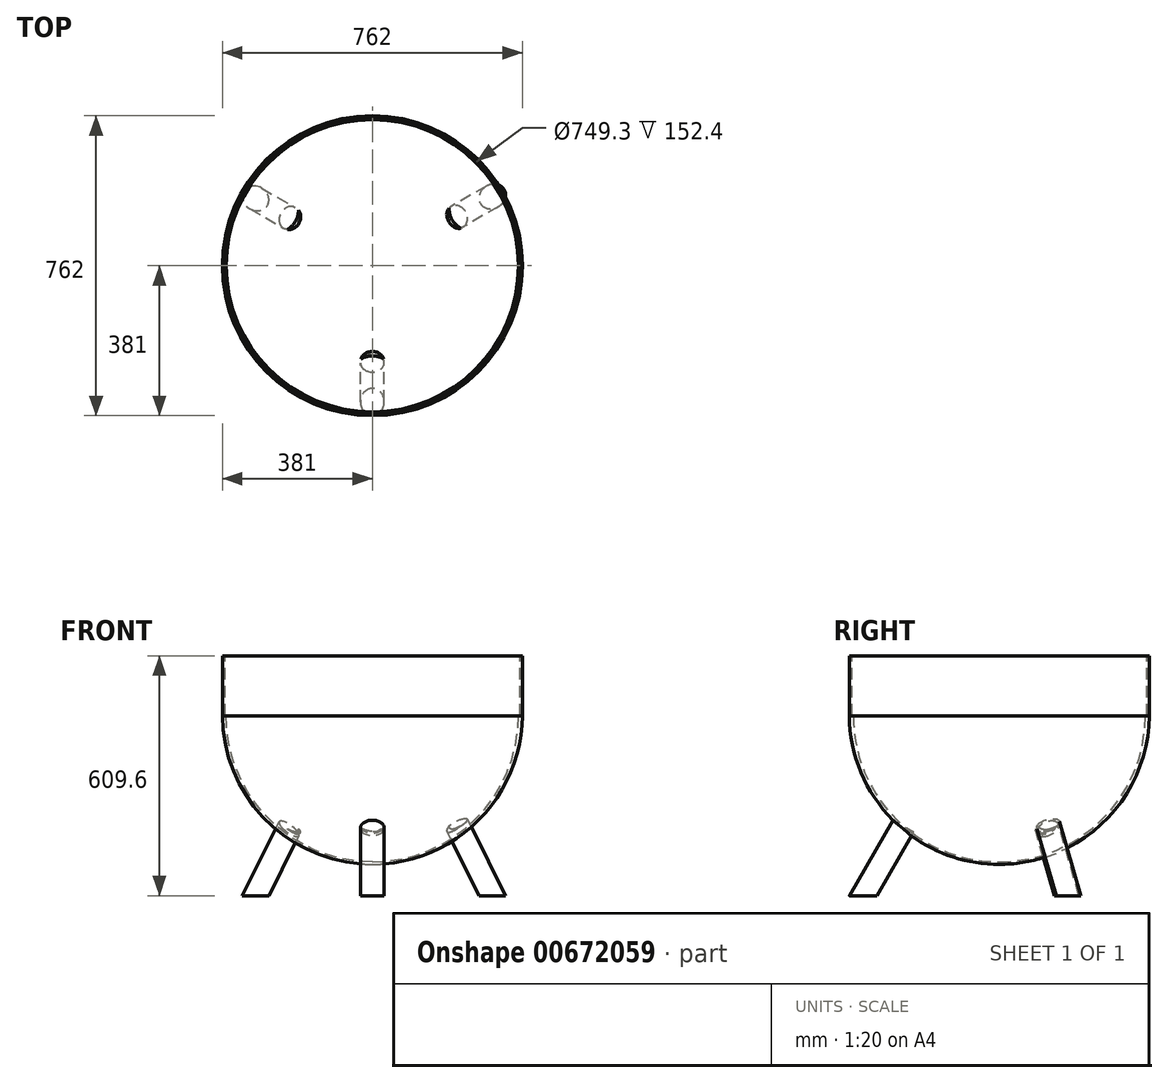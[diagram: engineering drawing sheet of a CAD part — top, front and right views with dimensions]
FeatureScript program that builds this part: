
annotation { "Feature Type Name" : "Feature", "Feature Type Description" : "" }
export const myFeature = defineFeature(function(context is Context, id is Id, definition is map)
    precondition{}
    {
        {
            var Q0;
            Q0=qCreatedBy(makeId("Top.planeOp"),FACE);
            var sketch = newSketch(context, id + "F0", { "sketchPlane" : qUnion([Q0])});
            skCircle(sketch, "E0.cCircle", {"center": v(0, 0) * mm, "radius": 527.93 * mm, "construction": true});
            skLineSegment(sketch, "E0.0", {"start": v(304.8, 527.93) * mm, "end": v(609.6, 0) * mm});
            skLineSegment(sketch, "E0.1", {"start": v(609.6, 0) * mm, "end": v(457.2, -263.96) * mm});
            skLineSegment(sketch, "E0.2", {"start": v(304.8, -527.93) * mm, "end": v(-304.8, -527.93) * mm});
            skLineSegment(sketch, "E0.3", {"start": v(-304.8, -527.93) * mm, "end": v(-457.2, -263.96) * mm});
            skLineSegment(sketch, "E0.4", {"start": v(-609.6, 0) * mm, "end": v(-450.85, 274.96) * mm});
            skLineSegment(sketch, "E0.5", {"start": v(-304.8, 527.93) * mm, "end": v(0, 527.93) * mm});
            skPoint(sketch, "E0.0.midPoint", {"position": v(457.2, 263.96) * mm});
            skCircle(sketch, "E1", {"center": v(0, 0) * mm, "radius": 381 * mm});
            skLineSegment(sketch, "E2", {"start": v(-463.55, 252.97) * mm, "end": v(-336.12, 179.4) * mm});
            skLineSegment(sketch, "E3", {"start": v(-450.85, 274.96) * mm, "end": v(-323.42, 201.4) * mm});
            skLineSegment(sketch, "E4", {"start": v(-304.8, 527.93) * mm, "end": v(-304.8, 527.93) * mm});
            skLineSegment(sketch, "E5", {"start": v(-463.55, 252.97) * mm, "end": v(-304.8, 527.93) * mm});
            skLineSegment(sketch, "E6", {"start": v(-450.85, 274.96) * mm, "end": v(-401.2, 360.95) * mm});
            skLineSegment(sketch, "E7", {"start": v(-609.6, 0) * mm, "end": v(-609.6, 0) * mm});
            skLineSegment(sketch, "E8.1.0", {"start": v(-450.85, -274.96) * mm, "end": v(-323.42, -201.4) * mm});
            skLineSegment(sketch, "E8.1.1", {"start": v(-463.55, -252.97) * mm, "end": v(-336.12, -179.4) * mm});
            skLineSegment(sketch, "E8.2.0", {"start": v(12.7, -527.93) * mm, "end": v(12.7, -380.79) * mm});
            skLineSegment(sketch, "E8.2.1", {"start": v(-12.7, -527.93) * mm, "end": v(-12.7, -380.79) * mm});
            skLineSegment(sketch, "E8.3.0", {"start": v(463.55, -252.97) * mm, "end": v(336.12, -179.4) * mm});
            skLineSegment(sketch, "E8.3.1", {"start": v(450.85, -274.96) * mm, "end": v(323.42, -201.4) * mm});
            skLineSegment(sketch, "E8.4.0", {"start": v(450.85, 274.96) * mm, "end": v(323.42, 201.4) * mm});
            skLineSegment(sketch, "E8.4.1", {"start": v(463.55, 252.97) * mm, "end": v(336.12, 179.4) * mm});
            skLineSegment(sketch, "E8.5.0", {"start": v(-12.7, 527.93) * mm, "end": v(-12.7, 380.79) * mm});
            skLineSegment(sketch, "E8.5.1", {"start": v(12.7, 527.93) * mm, "end": v(12.7, 380.79) * mm});
            skLineSegment(sketch, "E9", {"start": v(-1099.5, 381) * mm, "end": v(1284.02, 381) * mm, "construction": true});
            skLineSegment(sketch, "E10", {"start": v(-1101.82, -381) * mm, "end": v(1466.6, -381) * mm, "construction": true});
            skLineSegment(sketch, "E11", {"start": v(127, -73.32) * mm, "end": v(-127, -73.32) * mm});
            skCircle(sketch, "E12", {"center": v(0, 0) * mm, "radius": 146.65 * mm, "construction": true});
            skLineSegment(sketch, "E13", {"start": v(0, 0) * mm, "end": v(329.96, -190.5) * mm, "construction": true});
            skLineSegment(sketch, "E14", {"start": v(0, 0) * mm, "end": v(-329.96, -190.5) * mm, "construction": true});
            skLineSegment(sketch, "E15", {"start": v(0, 0) * mm, "end": v(0, 381) * mm, "construction": true});
            skLineSegment(sketch, "E16", {"start": v(329.96, -190.5) * mm, "end": v(1171.58, -676.41) * mm, "construction": true});
            skLineSegment(sketch, "E17", {"start": v(457.2, -263.96) * mm, "end": v(304.8, -527.93) * mm});
            skLineSegment(sketch, "E18", {"start": v(329.96, -190.5) * mm, "end": v(457.2, -263.96) * mm});
            skLineSegment(sketch, "E19", {"start": v(0, 381) * mm, "end": v(0, 1090.4) * mm, "construction": true});
            skLineSegment(sketch, "E20", {"start": v(0, 527.93) * mm, "end": v(304.8, 527.93) * mm});
            skLineSegment(sketch, "E21", {"start": v(0, 527.93) * mm, "end": v(0, 381) * mm});
            skLineSegment(sketch, "E22", {"start": v(-329.96, -190.5) * mm, "end": v(-1262.9, -729.14) * mm, "construction": true});
            skLineSegment(sketch, "E23", {"start": v(-457.2, -263.96) * mm, "end": v(-609.6, 0) * mm});
            skLineSegment(sketch, "E24", {"start": v(-329.96, -190.5) * mm, "end": v(-457.2, -263.96) * mm});
            skCircle(sketch, "E25", {"center": v(0, 0) * mm, "radius": 374.65 * mm});
            skSolve(sketch);
        }
        {
            var Q0;
            {var subQ0=sQuery(id+"F0.wireOp",EDGE,"E1");var subQ8=makeQuery(id+"F0.imprint","INTERSECT",VERTEX,{"derivedFrom":[subQ0,sQuery(id+"F0.wireOp",EDGE,"E8.4.0")]});Q0=makeQuery(id+"F0.imprint","IMPRINT",FACE,{"disambiguationData":[TD([[makeQuery(id+"F0.imprint","IMPRINT",EDGE,{"disambiguationData":[TD([[subQ8,1.0]])],"derivedFrom":subQ0}),1.0]])]});}
            extrude(context, id + "F1", {"entities" : qUnion([Q0]), "oppositeDirection" : true, "depth" : 152.4 * mm, "offsetDistance" : 25.4 * mm, "hasSecondDirection" : true, "secondDirectionOppositeDirection" : true, "secondDirectionDepth" : 0 * mm});
        }
        {
            var Q0;
            Q0=qCreatedBy(makeId("Front.planeOp"),FACE);
            var sketch = newSketch(context, id + "F2", { "sketchPlane" : qUnion([Q0])});
            skLineSegment(sketch, "E26", {"start": v(0, 608.83) * mm, "end": v(0, -1105.26) * mm, "construction": true});
            skLineSegment(sketch, "E27", {"start": v(-381, 462.6) * mm, "end": v(-381, -843.09) * mm});
            skLineSegment(sketch, "E28.MirrorCS", {"start": v(381, 462.6) * mm, "end": v(381, -843.09) * mm});
            skLineSegment(sketch, "E29", {"start": v(-1108.33, -152.4) * mm, "end": v(1492.5, -152.4) * mm, "construction": true});
            skArc(sketch, "E30", {"start": v(-381, -152.4) * mm, "mid": v(-268.19, -419.57) * mm, "end": v(0, -529.94) * mm});
            skArc(sketch, "E31", {"start": v(0, -529.94) * mm, "mid": v(268.19, -419.57) * mm, "end": v(381, -152.4) * mm});
            skLineSegment(sketch, "E32", {"start": v(-495.68, -152.4) * mm, "end": v(0, -152.4) * mm});
            skLineSegment(sketch, "E33", {"start": v(0, 45.3) * mm, "end": v(0, -541.67) * mm});
            skLineSegment(sketch, "E34", {"start": v(0, -152.4) * mm, "end": v(518.85, -152.4) * mm});
            skCircle(sketch, "E35", {"center": v(0, -152.4) * mm, "radius": 371.19 * mm});
            skSolve(sketch);
        }
        {
            var Q0;
            Q0=sQuery(id+"F0.wireOp",EDGE,"E13");
            var Q1;
            Q1=sQuery(id+"F2.wireOp",EDGE,"E26");
            cPlane(context, id + "F3", {"entities" : qUnion([Q0, Q1]), "cplaneType" : CPlaneType.LINE_ANGLE, "offset" : 25.4 * mm, "angle" : 0 * degree, "width" : 152.4 * mm, "height" : 152.4 * mm});
        }
        {
            var Q0;
            Q0=sQuery(id+"F0.wireOp",EDGE,"E15");
            var Q1;
            Q1=sQuery(id+"F2.wireOp",EDGE,"E26");
            cPlane(context, id + "F4", {"entities" : qUnion([Q0, Q1]), "cplaneType" : CPlaneType.LINE_ANGLE, "offset" : 25.4 * mm, "angle" : 0 * degree, "width" : 152.4 * mm, "height" : 152.4 * mm});
        }
        {
            var Q0;
            Q0=sQuery(id+"F0.wireOp",EDGE,"E22");
            var Q1;
            Q1=sQuery(id+"F2.wireOp",EDGE,"E26");
            cPlane(context, id + "F5", {"entities" : qUnion([Q0, Q1]), "cplaneType" : CPlaneType.LINE_ANGLE, "offset" : 25.4 * mm, "angle" : 0 * degree, "width" : 152.4 * mm, "height" : 152.4 * mm});
        }
        {
            var Q0;
            Q0=qCreatedBy(id+"F5.planeOp",FACE);
            var sketch = newSketch(context, id + "F6", { "sketchPlane" : qUnion([Q0])});
            skLineSegment(sketch, "E36", {"start": v(-1017.96, -609.6) * mm, "end": v(-351.95, -609.6) * mm});
            skLineSegment(sketch, "E37", {"start": v(-2207.22, 0) * mm, "end": v(364.68, 0) * mm, "construction": true});
            skLineSegment(sketch, "E38", {"start": v(0, 853.8) * mm, "end": v(0, -860.28) * mm, "construction": true});
            skLineSegment(sketch, "E39", {"start": v(-381, 707.57) * mm, "end": v(-381, -944.4) * mm});
            skLineSegment(sketch, "E40", {"start": v(-2225.52, -152.4) * mm, "end": v(0, -152.4) * mm, "construction": true});
            skArc(sketch, "E41", {"start": v(-381, -152.4) * mm, "mid": v(-268.19, -419.57) * mm, "end": v(0, -529.94) * mm});
            skArc(sketch, "E42", {"start": v(0, -529.94) * mm, "mid": v(268.19, -419.57) * mm, "end": v(381, -152.4) * mm});
            skLineSegment(sketch, "E43", {"start": v(0, -152.4) * mm, "end": v(375.32, -152.4) * mm, "construction": true});
            skLineSegment(sketch, "E44", {"start": v(-1487.46, 0) * mm, "end": v(0, 0) * mm, "construction": true});
            skLineSegment(sketch, "E45", {"start": v(-470.85, 0) * mm, "end": v(0, 0) * mm, "construction": true});
            skLineSegment(sketch, "E46", {"start": v(277.13, -609.6) * mm, "end": v(310.58, -609.6) * mm});
            skLineSegment(sketch, "E47", {"start": v(0, 0) * mm, "end": v(-351.95, -609.6) * mm});
            skLineSegment(sketch, "E48", {"start": v(32.55, -3.98) * mm, "end": v(-317.1, -609.6) * mm});
            skLineSegment(sketch, "E49", {"start": v(-34.84, 0) * mm, "end": v(-386.8, -609.6) * mm});
            skLineSegment(sketch, "E50", {"start": v(-381, -609.6) * mm, "end": v(1871, -609.6) * mm});
            skLineSegment(sketch, "E51.MirrorCS", {"start": v(34.84, 0) * mm, "end": v(386.8, -609.6) * mm});
            skLineSegment(sketch, "E52.MirrorCS", {"start": v(-32.55, -3.98) * mm, "end": v(317.1, -609.6) * mm});
            skLineSegment(sketch, "E53.MirrorCS", {"start": v(0, 0) * mm, "end": v(351.95, -609.6) * mm});
            skSolve(sketch);
        }
        {
            var Q0;
            {var subQ0=sQuery(id+"F6.wireOp",EDGE,"E51.MirrorCS");var subQ1=sQuery(id+"F6.wireOp",EDGE,"E42");var subQ2=makeQuery(id+"F6.imprint","INTERSECT",VERTEX,{"derivedFrom":[subQ1,subQ0]});Q0=makeQuery(id+"F6.imprint","IMPRINT",FACE,{"disambiguationData":[TD([[makeQuery(id+"F6.imprint","IMPRINT",EDGE,{"disambiguationData":[TD([[subQ2,1.0]])],"derivedFrom":subQ1}),-1.0]])]});}
            var Q1;
            Q1=sQuery(id+"F6.wireOp",EDGE,"E53.MirrorCS");
            revolve(context, id + "F7", {"entities" : qUnion([Q0]), "axis" : qUnion([Q1]), "revolveType" : RevolveType.FULL});
        }
        {
            var Q0;
            {var subQ0=sQuery(id+"F2.wireOp",EDGE,"E31");Q0=makeQuery(id+"F2.imprint","IMPRINT",FACE,{"disambiguationData":[TD([[makeQuery(id+"F2.imprint","IMPRINT",EDGE,{"derivedFrom":subQ0}),1.0]])]});}
            var Q1;
            Q1=sQuery(id+"F2.wireOp",EDGE,"E33");
            revolve(context, id + "F8", {"entities" : qUnion([Q0]), "axis" : qUnion([Q1]), "revolveType" : RevolveType.FULL});
        }
        {
            var Q0;
            {var subQ0=sQuery(id+"F2.wireOp",EDGE,"E34");var subQ3=sQuery(id+"F2.wireOp",EDGE,"E35");var subQ5=makeQuery(id+"F2.imprint","INTERSECT",VERTEX,{"derivedFrom":[subQ0,subQ3]});Q0=makeQuery(id+"F2.imprint","IMPRINT",FACE,{"disambiguationData":[TD([[makeQuery(id+"F2.imprint","IMPRINT",EDGE,{"disambiguationData":[TD([[subQ5,1.0]])],"derivedFrom":subQ3}),1.0]])]});}
            var Q1;
            Q1=sQuery(id+"F2.wireOp",EDGE,"E33");
            revolve(context, id + "F9", {"operationType" : NewBodyOperationType.REMOVE, "entities" : qUnion([Q0]), "axis" : qUnion([Q1]), "revolveType" : RevolveType.FULL, "oppositeDirection" : true});
        }
        {
            var Q0;
            {var subQ0=sQuery(id+"F0.wireOp",EDGE,"E8.1.0");Q0=makeQuery(id+"F0.imprint","IMPRINT",FACE,{"disambiguationData":[TD([[makeQuery(id+"F0.imprint","IMPRINT",EDGE,{"derivedFrom":subQ0}),-1.0]])]});}
            cPlane(context, id + "F10", {"entities" : qUnion([Q0]), "cplaneType" : CPlaneType.OFFSET, "offset" : 647.7 * mm, "oppositeDirection" : true, "width" : 152.4 * mm, "height" : 152.4 * mm});
        }
        {
            var Q0;
            Q0=qCreatedBy(id+"F10.planeOp",FACE);
            var sketch = newSketch(context, id + "F11", { "sketchPlane" : qUnion([Q0])});
            skLineSegment(sketch, "E54.bottom", {"start": v(-408.5, 256.07) * mm, "end": v(423.7, 256.07) * mm});
            skLineSegment(sketch, "E54.top", {"start": v(-408.5, -410.84) * mm, "end": v(423.7, -410.84) * mm});
            skLineSegment(sketch, "E54.left", {"start": v(-408.5, 256.07) * mm, "end": v(-408.5, -410.84) * mm});
            skLineSegment(sketch, "E54.right", {"start": v(423.7, 256.07) * mm, "end": v(423.7, -410.84) * mm});
            skSolve(sketch);
        }
        {
            var Q0;
            Q0=qSketchRegion(id+"F11",true);
            extrude(context, id + "F12", {"entities" : qUnion([Q0]), "operationType" : NewBodyOperationType.REMOVE, "oppositeDirection" : true, "depth" : 50.8 * mm, "offsetDistance" : 25.4 * mm});
        }
        {
            var Q0;
            Q0=qCreatedBy(id+"F3.planeOp",FACE);
            var sketch = newSketch(context, id + "F13", { "sketchPlane" : qUnion([Q0])});
            skLineSegment(sketch, "E55", {"start": v(-1049.37, -609.6) * mm, "end": v(-342.54, -609.6) * mm});
            skLineSegment(sketch, "E56", {"start": v(-2238.63, 0) * mm, "end": v(333.27, 0) * mm, "construction": true});
            skLineSegment(sketch, "E57", {"start": v(0, 853.8) * mm, "end": v(0, -860.28) * mm, "construction": true});
            skLineSegment(sketch, "E58", {"start": v(-381, 707.57) * mm, "end": v(-381, -944.4) * mm});
            skLineSegment(sketch, "E59", {"start": v(-2225.52, -152.4) * mm, "end": v(0, -152.4) * mm, "construction": true});
            skArc(sketch, "E60", {"start": v(-381, -152.4) * mm, "mid": v(-268.19, -419.57) * mm, "end": v(0, -529.94) * mm});
            skArc(sketch, "E61", {"start": v(0, -529.94) * mm, "mid": v(268.19, -419.57) * mm, "end": v(381, -152.4) * mm});
            skLineSegment(sketch, "E62", {"start": v(0, -152.4) * mm, "end": v(375.32, -152.4) * mm, "construction": true});
            skLineSegment(sketch, "E63", {"start": v(-1518.87, 0) * mm, "end": v(0, 0) * mm, "construction": true});
            skLineSegment(sketch, "E64", {"start": v(-502.26, 0) * mm, "end": v(0, 0) * mm, "construction": true});
            skLineSegment(sketch, "E65", {"start": v(245.72, -609.6) * mm, "end": v(310.58, -609.6) * mm});
            skLineSegment(sketch, "E66", {"start": v(9.41, 0) * mm, "end": v(-342.54, -609.6) * mm});
            skLineSegment(sketch, "E67", {"start": v(63.96, 34.12) * mm, "end": v(-307.7, -609.6) * mm});
            skLineSegment(sketch, "E68", {"start": v(-25.43, 0) * mm, "end": v(-377.38, -609.6) * mm});
            skLineSegment(sketch, "E69", {"start": v(-381, -609.6) * mm, "end": v(1839.6, -609.6) * mm});
            skLineSegment(sketch, "E70.MirrorCS", {"start": v(25.43, 0) * mm, "end": v(377.38, -609.6) * mm});
            skLineSegment(sketch, "E71.MirrorCS", {"start": v(-63.96, 34.12) * mm, "end": v(307.7, -609.6) * mm});
            skLineSegment(sketch, "E72.MirrorCS", {"start": v(-9.41, 0) * mm, "end": v(342.54, -609.6) * mm});
            skSolve(sketch);
        }
        {
            var Q0;
            {var subQ0=sQuery(id+"F13.wireOp",EDGE,"E70.MirrorCS");var subQ1=sQuery(id+"F13.wireOp",EDGE,"E61");var subQ2=makeQuery(id+"F13.imprint","INTERSECT",VERTEX,{"derivedFrom":[subQ1,subQ0]});Q0=makeQuery(id+"F13.imprint","IMPRINT",FACE,{"disambiguationData":[TD([[makeQuery(id+"F13.imprint","IMPRINT",EDGE,{"disambiguationData":[TD([[subQ2,1.0]])],"derivedFrom":subQ1}),-1.0]])]});}
            var Q1;
            Q1=sQuery(id+"F13.wireOp",EDGE,"E72.MirrorCS");
            revolve(context, id + "F14", {"operationType" : NewBodyOperationType.ADD, "entities" : qUnion([Q0]), "axis" : qUnion([Q1]), "revolveType" : RevolveType.FULL});
        }
        {
            var Q0;
            Q0=qCreatedBy(id+"F4.planeOp",FACE);
            var sketch = newSketch(context, id + "F15", { "sketchPlane" : qUnion([Q0])});
            skLineSegment(sketch, "E73", {"start": v(-1075.54, -609.6) * mm, "end": v(-346.16, -609.6) * mm});
            skLineSegment(sketch, "E74", {"start": v(-2264.8, 0) * mm, "end": v(307.1, 0) * mm, "construction": true});
            skLineSegment(sketch, "E75", {"start": v(0, 1137.28) * mm, "end": v(0, -576.81) * mm, "construction": true});
            skLineSegment(sketch, "E76", {"start": v(-381, 707.57) * mm, "end": v(-381, -944.4) * mm});
            skLineSegment(sketch, "E77", {"start": v(-2225.52, -152.4) * mm, "end": v(0, -152.4) * mm, "construction": true});
            skArc(sketch, "E78", {"start": v(-381, -152.4) * mm, "mid": v(-268.19, -419.57) * mm, "end": v(0, -529.94) * mm});
            skArc(sketch, "E79", {"start": v(0, -529.94) * mm, "mid": v(268.19, -419.57) * mm, "end": v(381, -152.4) * mm});
            skLineSegment(sketch, "E80", {"start": v(0, -152.4) * mm, "end": v(375.32, -152.4) * mm, "construction": true});
            skLineSegment(sketch, "E81", {"start": v(-1545.05, 0) * mm, "end": v(0, 0) * mm, "construction": true});
            skLineSegment(sketch, "E82", {"start": v(-528.43, 0) * mm, "end": v(0, 0) * mm, "construction": true});
            skLineSegment(sketch, "E83", {"start": v(219.55, -609.6) * mm, "end": v(310.58, -609.6) * mm});
            skLineSegment(sketch, "E84", {"start": v(5.8, 0) * mm, "end": v(-346.16, -609.6) * mm});
            skLineSegment(sketch, "E85", {"start": v(67.79, 47.02) * mm, "end": v(-311.31, -609.6) * mm});
            skLineSegment(sketch, "E86", {"start": v(-29.05, 0) * mm, "end": v(-381, -609.6) * mm});
            skLineSegment(sketch, "E87", {"start": v(-381, -609.6) * mm, "end": v(1813.42, -609.6) * mm});
            skLineSegment(sketch, "E88.MirrorCS", {"start": v(29.05, 0) * mm, "end": v(381, -609.6) * mm});
            skLineSegment(sketch, "E89.MirrorCS", {"start": v(-67.79, 47.02) * mm, "end": v(311.31, -609.6) * mm});
            skLineSegment(sketch, "E90.MirrorCS", {"start": v(-5.8, 0) * mm, "end": v(346.16, -609.6) * mm});
            skLineSegment(sketch, "E91.bottom", {"start": v(381, 0) * mm, "end": v(566.13, 0) * mm});
            skLineSegment(sketch, "E91.top", {"start": v(381, -609.6) * mm, "end": v(579.4, -609.6) * mm});
            skLineSegment(sketch, "E91.left", {"start": v(381, 0) * mm, "end": v(381, -381) * mm});
            skLineSegment(sketch, "E91.right", {"start": v(566.13, 0) * mm, "end": v(566.13, -450.09) * mm});
            skLineSegment(sketch, "E92", {"start": v(282.01, -438.15) * mm, "end": v(381, -381) * mm});
            skLineSegment(sketch, "E93", {"start": v(358.21, -570.13) * mm, "end": v(381, -556.98) * mm});
            skLineSegment(sketch, "E94", {"start": v(381, -556.98) * mm, "end": v(566.13, -450.09) * mm});
            skSolve(sketch);
        }
        {
            var Q0;
            {var subQ0=sQuery(id+"F15.wireOp",EDGE,"E88.MirrorCS");var subQ1=sQuery(id+"F15.wireOp",EDGE,"E79");var subQ2=makeQuery(id+"F15.imprint","INTERSECT",VERTEX,{"derivedFrom":[subQ1,subQ0]});Q0=makeQuery(id+"F15.imprint","IMPRINT",FACE,{"disambiguationData":[TD([[makeQuery(id+"F15.imprint","IMPRINT",EDGE,{"disambiguationData":[TD([[subQ2,1.0]])],"derivedFrom":subQ1}),-1.0]])]});}
            var Q1;
            Q1=sQuery(id+"F15.wireOp",EDGE,"E90.MirrorCS");
            revolve(context, id + "F16", {"operationType" : NewBodyOperationType.ADD, "entities" : qUnion([Q0]), "axis" : qUnion([Q1]), "revolveType" : RevolveType.FULL});
        }
        {
            var Q0;
            Q0 = qSketchRegion(id + "F11", true);
            extrude(context, id + "F17", {"entities" : qUnion([Q0]), "operationType" : NewBodyOperationType.REMOVE, "oppositeDirection" : true, "depth" : 50.8 * mm, "offsetDistance" : 25.4 * mm, "hasSecondDirection" : true, "secondDirectionOppositeDirection" : true, "secondDirectionDepth" : -38.1 * mm});
        }
    });
